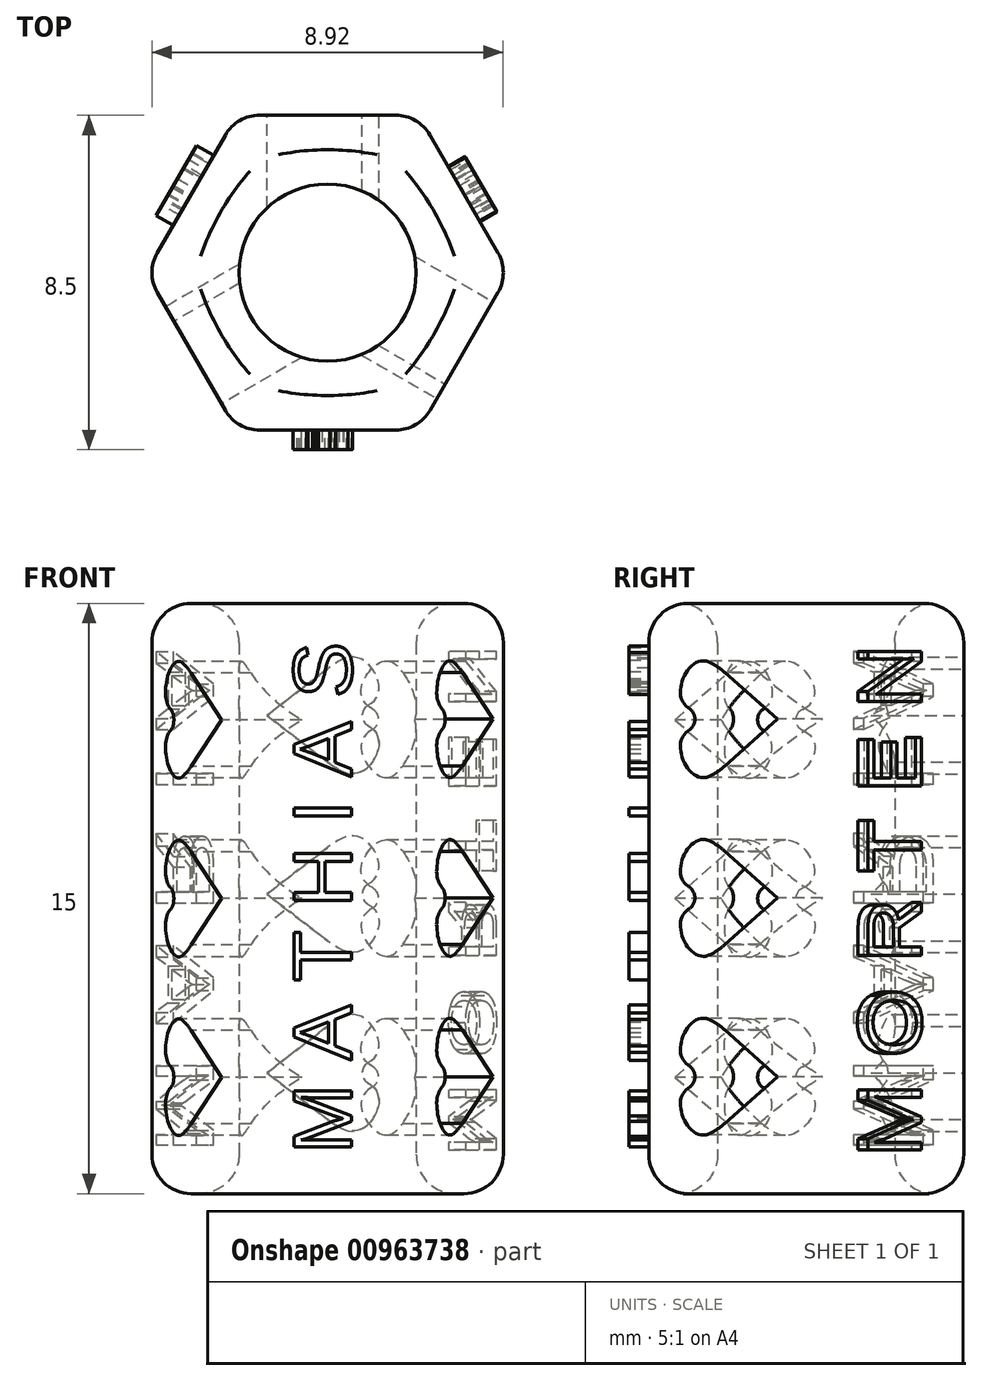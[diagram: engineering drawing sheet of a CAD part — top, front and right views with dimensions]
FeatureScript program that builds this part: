
annotation { "Feature Type Name" : "Feature", "Feature Type Description" : "" }
export const myFeature = defineFeature(function(context is Context, id is Id, definition is map)
    precondition{}
    {
        {
            var Q0;
            Q0=qCreatedBy(makeId("Top.planeOp"),FACE);
            var sketch = newSketch(context, id + "F0", { "sketchPlane" : qUnion([Q0])});
            skCircle(sketch, "E0", {"center": v(0, 0) * mm, "radius": 2.25 * mm});
            skCircle(sketch, "E1.cCircle", {"center": v(0, 0) * mm, "radius": 4 * mm, "construction": true});
            skLineSegment(sketch, "E1.0", {"start": v(2.3, -4) * mm, "end": v(-2.3, -4) * mm});
            skLineSegment(sketch, "E1.1", {"start": v(-2.3, -4) * mm, "end": v(-4.62, 0) * mm});
            skLineSegment(sketch, "E1.2", {"start": v(-4.62, 0) * mm, "end": v(-2.3, 4) * mm});
            skLineSegment(sketch, "E1.3", {"start": v(-2.3, 4) * mm, "end": v(2.3, 4) * mm});
            skLineSegment(sketch, "E1.4", {"start": v(2.3, 4) * mm, "end": v(4.62, 0) * mm});
            skLineSegment(sketch, "E1.5", {"start": v(4.62, 0) * mm, "end": v(2.3, -4) * mm});
            skPoint(sketch, "E1.0.midPoint", {"position": v(0, -4) * mm});
            skSolve(sketch);
        }
        {
            var Q0;
            Q0=makeQuery(id+"F0.imprint","IMPRINT",FACE,{"disambiguationData":[TD([[makeQuery(id+"F0.imprint","IMPRINT",EDGE,{"derivedFrom":sQuery(id+"F0.wireOp",EDGE,"E0")}),-1.0]])]});
            extrude(context, id + "F1", {"entities" : qUnion([Q0]), "depth" : 15 * mm, "offsetDistance" : 25 * mm});
        }
        {
            var Q0;
            Q0=makeQuery(id+"F1.opExtrude","SWEPT_FACE",FACE,{"disambiguationData":[OSD([sQuery(id+"F0.wireOp",EDGE,"E1.2")])]});
            var sketch = newSketch(context, id + "F2", { "sketchPlane" : qUnion([Q0])});
            skText(sketch, "E2", { "text": "M A R I A", "fontName": "Arimo-Regular.ttf"});
            skPoint(sketch, "E3", {"position": v(-2.3, 7.5) * mm});
            const initialGuessF2  = {"E2": [0.00092, 0.001, 0, 1, 0.00215]};
            skSetInitialGuess(sketch, initialGuessF2);
            skSolve(sketch);
        }
        {
            var Q0;
            Q0 = qSketchRegion(id + "F2", true);
            extrude(context, id + "F3", {"entities" : qUnion([Q0]), "operationType" : NewBodyOperationType.ADD, "depth" : 0.5 * mm, "offsetDistance" : 25 * mm});
        }
        {
            var Q0;
            Q0=makeQuery(id+"F1.opExtrude","SWEPT_FACE",FACE,{"disambiguationData":[OSD([sQuery(id+"F0.wireOp",EDGE,"E1.4")])]});
            var sketch = newSketch(context, id + "F4", { "sketchPlane" : qUnion([Q0])});
            skText(sketch, "E4", { "text": "M O R T E N", "fontName": "Arimo-Regular.ttf"});
            const initialGuessF4  = {"E4": [0.00078, 0.00093, 0, 1, 0.00164]};
            skSetInitialGuess(sketch, initialGuessF4);
            skSolve(sketch);
        }
        {
            var Q0;
            Q0 = qSketchRegion(id + "F4", true);
            extrude(context, id + "F5", {"entities" : qUnion([Q0]), "operationType" : NewBodyOperationType.ADD, "depth" : 0.5 * mm, "offsetDistance" : 25 * mm});
        }
        {
            var Q0;
            Q0=makeQuery(id+"F1.opExtrude","SWEPT_FACE",FACE,{"disambiguationData":[OSD([sQuery(id+"F0.wireOp",EDGE,"E1.0")])]});
            var sketch = newSketch(context, id + "F6", { "sketchPlane" : qUnion([Q0])});
            skText(sketch, "E5", { "text": "M A T H I A S", "fontName": "Arimo-Regular.ttf"});
            const initialGuessF6  = {"E5": [0.00061, 0.00102, 0, 1, 0.00153]};
            skSetInitialGuess(sketch, initialGuessF6);
            skSolve(sketch);
        }
        {
            var Q0;
            Q0 = qSketchRegion(id + "F6", true);
            extrude(context, id + "F7", {"entities" : qUnion([Q0]), "operationType" : NewBodyOperationType.ADD, "depth" : 0.5 * mm, "offsetDistance" : 25 * mm});
        }
        {
            var Q0;
            Q0=makeQuery(id+"F1.opExtrude","SWEPT_FACE",FACE,{"disambiguationData":[OSD([sQuery(id+"F0.wireOp",EDGE,"E1.1")])]});
            var sketch = newSketch(context, id + "F8", { "sketchPlane" : qUnion([Q0])});
            skLineSegment(sketch, "E6", {"start": v(2.3, 0) * mm, "end": v(-2.3, 15) * mm, "construction": true});
            skLineSegment(sketch, "E7", {"start": v(-2.3, 15) * mm, "end": v(0, 7.5) * mm, "construction": true});
            skLineSegment(sketch, "E8", {"start": v(0, 7.5) * mm, "end": v(1.54, 7.5) * mm, "construction": true});
            skLineSegment(sketch, "E9", {"start": v(1.54, 7.5) * mm, "end": v(0, 8.68) * mm});
            skFitSpline(sketch, "E10", {"points": [v(0, 8.68) * mm, v(-0.64, 8.98) * mm, v(-1.14, 8.68) * mm, v(-1.3, 8.14) * mm, v(-1.11, 7.81) * mm, v(-0.57, 7.6) * mm, v(0, 7.5) * mm], "startDerivative": vector(-3.48, 2.43) * mm, "endDerivative": vector(3.32, -0.48) * mm});
            skLineSegment(sketch, "E11.MirrorCS", {"start": v(1.54, 7.5) * mm, "end": v(0, 6.32) * mm});
            skFitSpline(sketch, "E12.MirrorCS", {"points": [v(0, 6.32) * mm, v(-0.64, 6.02) * mm, v(-1.14, 6.32) * mm, v(-1.3, 6.86) * mm, v(-1.11, 7.19) * mm, v(-0.57, 7.4) * mm, v(0, 7.5) * mm], "startDerivative": vector(-3.48, -2.43) * mm, "endDerivative": vector(3.32, 0.48) * mm});
            skLineSegment(sketch, "E13", {"start": v(2.3, 4.54) * mm, "end": v(-2.3, 19.54) * mm, "construction": true});
            skLineSegment(sketch, "E14", {"start": v(-2.3, 19.54) * mm, "end": v(0, 12.04) * mm, "construction": true});
            skLineSegment(sketch, "E15", {"start": v(0, 12.04) * mm, "end": v(1.54, 12.04) * mm, "construction": true});
            skLineSegment(sketch, "E16", {"start": v(1.54, 12.04) * mm, "end": v(0, 13.22) * mm});
            skFitSpline(sketch, "E17", {"points": [v(0, 13.22) * mm, v(-0.64, 13.52) * mm, v(-1.14, 13.22) * mm, v(-1.3, 12.68) * mm, v(-1.11, 12.35) * mm, v(-0.57, 12.14) * mm, v(0, 12.04) * mm], "startDerivative": vector(-3.48, 2.43) * mm, "endDerivative": vector(3.32, -0.48) * mm});
            skLineSegment(sketch, "E18.MirrorCS", {"start": v(1.54, 12.04) * mm, "end": v(0, 10.86) * mm});
            skFitSpline(sketch, "E19.MirrorCS", {"points": [v(0, 10.86) * mm, v(-0.64, 10.56) * mm, v(-1.14, 10.86) * mm, v(-1.3, 11.4) * mm, v(-1.11, 11.73) * mm, v(-0.57, 11.94) * mm, v(0, 12.04) * mm], "startDerivative": vector(-3.48, -2.43) * mm, "endDerivative": vector(3.32, 0.48) * mm});
            skLineSegment(sketch, "E20.MirrorCS", {"start": v(1.54, 2.96) * mm, "end": v(0, 1.78) * mm});
            skLineSegment(sketch, "E21.MirrorCS", {"start": v(1.54, 2.96) * mm, "end": v(0, 4.14) * mm});
            skFitSpline(sketch, "E22.MirrorCS", {"points": [v(0, 4.14) * mm, v(-0.64, 4.44) * mm, v(-1.14, 4.14) * mm, v(-1.3, 3.6) * mm, v(-1.11, 3.27) * mm, v(-0.57, 3.06) * mm, v(0, 2.96) * mm], "startDerivative": vector(-3.48, 2.43) * mm, "endDerivative": vector(3.32, -0.48) * mm});
            skFitSpline(sketch, "E23.MirrorCS", {"points": [v(0, 1.78) * mm, v(-0.64, 1.48) * mm, v(-1.14, 1.78) * mm, v(-1.3, 2.32) * mm, v(-1.11, 2.65) * mm, v(-0.57, 2.86) * mm, v(0, 2.96) * mm], "startDerivative": vector(-3.48, -2.43) * mm, "endDerivative": vector(3.32, 0.48) * mm});
            skSolve(sketch);
        }
        {
            var Q0;
            Q0=makeQuery(id+"F8.imprint","IMPRINT",FACE,{"disambiguationData":[TD([[makeQuery(id+"F8.imprint","IMPRINT",EDGE,{"derivedFrom":sQuery(id+"F8.wireOp",EDGE,"E20.MirrorCS")}),-1.0]])]});
            var Q1;
            Q1=makeQuery(id+"F8.imprint","IMPRINT",FACE,{"disambiguationData":[TD([[makeQuery(id+"F8.imprint","IMPRINT",EDGE,{"derivedFrom":sQuery(id+"F8.wireOp",EDGE,"E9")}),1.0]])]});
            var Q2;
            Q2=makeQuery(id+"F8.imprint","IMPRINT",FACE,{"disambiguationData":[TD([[makeQuery(id+"F8.imprint","IMPRINT",EDGE,{"derivedFrom":sQuery(id+"F8.wireOp",EDGE,"E16")}),1.0]])]});
            extrude(context, id + "F9", {"entities" : qUnion([Q0, Q1, Q2]), "operationType" : NewBodyOperationType.REMOVE, "oppositeDirection" : true, "depth" : 5 * mm, "offsetDistance" : 25 * mm});
        }
        {
            var Q0;
            Q0=makeQuery(id+"F1.opExtrude","SWEPT_FACE",FACE,{"disambiguationData":[OSD([sQuery(id+"F0.wireOp",EDGE,"E1.3")])]});
            var sketch = newSketch(context, id + "F10", { "sketchPlane" : qUnion([Q0])});
            skLineSegment(sketch, "E24", {"start": v(2.31, 0.1) * mm, "end": v(-2.3, 15.1) * mm, "construction": true});
            skLineSegment(sketch, "E25", {"start": v(-2.3, 15.1) * mm, "end": v(0, 7.6) * mm, "construction": true});
            skLineSegment(sketch, "E26", {"start": v(0, 7.6) * mm, "end": v(1.54, 7.6) * mm, "construction": true});
            skLineSegment(sketch, "E27", {"start": v(1.54, 7.6) * mm, "end": v(0, 8.8) * mm});
            skFitSpline(sketch, "E28", {"points": [v(0, 8.8) * mm, v(-0.64, 9.1) * mm, v(-1.14, 8.8) * mm, v(-1.3, 8.25) * mm, v(-1.1, 7.92) * mm, v(-0.57, 7.7) * mm, v(0, 7.6) * mm], "startDerivative": vector(-3.48, 2.43) * mm, "endDerivative": vector(3.32, -0.48) * mm});
            skLineSegment(sketch, "E29.MirrorCS", {"start": v(1.54, 7.6) * mm, "end": v(0, 6.43) * mm});
            skFitSpline(sketch, "E30.MirrorCS", {"points": [v(0, 6.43) * mm, v(-0.64, 6.12) * mm, v(-1.14, 6.43) * mm, v(-1.3, 6.97) * mm, v(-1.1, 7.3) * mm, v(-0.57, 7.5) * mm, v(0, 7.6) * mm], "startDerivative": vector(-3.48, -2.43) * mm, "endDerivative": vector(3.32, 0.48) * mm});
            skLineSegment(sketch, "E31", {"start": v(2.31, 4.65) * mm, "end": v(-2.3, 19.65) * mm, "construction": true});
            skLineSegment(sketch, "E32", {"start": v(-2.3, 19.65) * mm, "end": v(0, 12.15) * mm, "construction": true});
            skLineSegment(sketch, "E33", {"start": v(0, 12.15) * mm, "end": v(1.54, 12.15) * mm, "construction": true});
            skLineSegment(sketch, "E34", {"start": v(1.54, 12.15) * mm, "end": v(0, 13.33) * mm});
            skFitSpline(sketch, "E35", {"points": [v(0, 13.33) * mm, v(-0.64, 13.63) * mm, v(-1.14, 13.33) * mm, v(-1.3, 12.8) * mm, v(-1.1, 12.46) * mm, v(-0.57, 12.25) * mm, v(0, 12.15) * mm], "startDerivative": vector(-3.48, 2.43) * mm, "endDerivative": vector(3.32, -0.48) * mm});
            skLineSegment(sketch, "E36.MirrorCS", {"start": v(1.54, 12.15) * mm, "end": v(0, 10.97) * mm});
            skFitSpline(sketch, "E37.MirrorCS", {"points": [v(0, 10.97) * mm, v(-0.64, 10.67) * mm, v(-1.14, 10.97) * mm, v(-1.3, 11.5) * mm, v(-1.1, 11.84) * mm, v(-0.57, 12.05) * mm, v(0, 12.15) * mm], "startDerivative": vector(-3.48, -2.43) * mm, "endDerivative": vector(3.32, 0.48) * mm});
            skLineSegment(sketch, "E38.MirrorCS", {"start": v(1.54, 3.07) * mm, "end": v(0, 1.89) * mm});
            skLineSegment(sketch, "E39.MirrorCS", {"start": v(1.54, 3.07) * mm, "end": v(0, 4.25) * mm});
            skFitSpline(sketch, "E40.MirrorCS", {"points": [v(0, 4.25) * mm, v(-0.64, 4.55) * mm, v(-1.14, 4.25) * mm, v(-1.3, 3.71) * mm, v(-1.1, 3.38) * mm, v(-0.57, 3.17) * mm, v(0, 3.07) * mm], "startDerivative": vector(-3.48, 2.43) * mm, "endDerivative": vector(3.32, -0.48) * mm});
            skFitSpline(sketch, "E41.MirrorCS", {"points": [v(0, 1.89) * mm, v(-0.64, 1.58) * mm, v(-1.14, 1.89) * mm, v(-1.3, 2.43) * mm, v(-1.1, 2.76) * mm, v(-0.57, 2.97) * mm, v(0, 3.07) * mm], "startDerivative": vector(-3.48, -2.43) * mm, "endDerivative": vector(3.32, 0.48) * mm});
            skSolve(sketch);
        }
        {
            var Q0;
            Q0 = qSketchRegion(id + "F10", true);
            extrude(context, id + "F11", {"entities" : qUnion([Q0]), "operationType" : NewBodyOperationType.REMOVE, "oppositeDirection" : true, "depth" : 5 * mm, "offsetDistance" : 25 * mm});
        }
        {
            var Q0;
            Q0=makeQuery(id+"F1.opExtrude","SWEPT_FACE",FACE,{"disambiguationData":[OSD([sQuery(id+"F0.wireOp",EDGE,"E1.5")])]});
            var sketch = newSketch(context, id + "F12", { "sketchPlane" : qUnion([Q0])});
            skLineSegment(sketch, "E42", {"start": v(2.24, 0.01) * mm, "end": v(-2.38, 15.01) * mm, "construction": true});
            skLineSegment(sketch, "E43", {"start": v(-2.38, 15.01) * mm, "end": v(-0.07, 7.51) * mm, "construction": true});
            skLineSegment(sketch, "E44", {"start": v(-0.07, 7.51) * mm, "end": v(1.46, 7.51) * mm, "construction": true});
            skLineSegment(sketch, "E45", {"start": v(1.46, 7.51) * mm, "end": v(-0.07, 8.7) * mm});
            skFitSpline(sketch, "E46", {"points": [v(-0.07, 8.7) * mm, v(-0.72, 9) * mm, v(-1.21, 8.7) * mm, v(-1.38, 8.16) * mm, v(-1.18, 7.82) * mm, v(-0.64, 7.61) * mm, v(-0.07, 7.51) * mm], "startDerivative": vector(-3.48, 2.43) * mm, "endDerivative": vector(3.32, -0.48) * mm});
            skLineSegment(sketch, "E47.MirrorCS", {"start": v(1.46, 7.51) * mm, "end": v(-0.07, 6.33) * mm});
            skFitSpline(sketch, "E48.MirrorCS", {"points": [v(-0.07, 6.33) * mm, v(-0.72, 6.03) * mm, v(-1.21, 6.33) * mm, v(-1.38, 6.87) * mm, v(-1.18, 7.2) * mm, v(-0.64, 7.41) * mm, v(-0.07, 7.51) * mm], "startDerivative": vector(-3.48, -2.43) * mm, "endDerivative": vector(3.32, 0.48) * mm});
            skLineSegment(sketch, "E49", {"start": v(2.24, 4.55) * mm, "end": v(-2.38, 19.55) * mm, "construction": true});
            skLineSegment(sketch, "E50", {"start": v(-2.38, 19.55) * mm, "end": v(-0.07, 12.05) * mm, "construction": true});
            skLineSegment(sketch, "E51", {"start": v(-0.07, 12.05) * mm, "end": v(1.46, 12.05) * mm, "construction": true});
            skLineSegment(sketch, "E52", {"start": v(1.46, 12.05) * mm, "end": v(-0.07, 13.24) * mm});
            skFitSpline(sketch, "E53", {"points": [v(-0.07, 13.24) * mm, v(-0.72, 13.54) * mm, v(-1.21, 13.24) * mm, v(-1.38, 12.7) * mm, v(-1.18, 12.36) * mm, v(-0.64, 12.15) * mm, v(-0.07, 12.05) * mm], "startDerivative": vector(-3.48, 2.43) * mm, "endDerivative": vector(3.32, -0.48) * mm});
            skLineSegment(sketch, "E54.MirrorCS", {"start": v(1.46, 12.05) * mm, "end": v(-0.07, 10.87) * mm});
            skFitSpline(sketch, "E55.MirrorCS", {"points": [v(-0.07, 10.87) * mm, v(-0.72, 10.57) * mm, v(-1.21, 10.87) * mm, v(-1.38, 11.41) * mm, v(-1.18, 11.74) * mm, v(-0.64, 11.95) * mm, v(-0.07, 12.05) * mm], "startDerivative": vector(-3.48, -2.43) * mm, "endDerivative": vector(3.32, 0.48) * mm});
            skLineSegment(sketch, "E56.MirrorCS", {"start": v(1.46, 2.97) * mm, "end": v(-0.07, 1.8) * mm});
            skLineSegment(sketch, "E57.MirrorCS", {"start": v(1.46, 2.97) * mm, "end": v(-0.07, 4.16) * mm});
            skFitSpline(sketch, "E58.MirrorCS", {"points": [v(-0.07, 4.16) * mm, v(-0.72, 4.46) * mm, v(-1.21, 4.16) * mm, v(-1.38, 3.61) * mm, v(-1.18, 3.28) * mm, v(-0.64, 3.07) * mm, v(-0.07, 2.97) * mm], "startDerivative": vector(-3.48, 2.43) * mm, "endDerivative": vector(3.32, -0.48) * mm});
            skFitSpline(sketch, "E59.MirrorCS", {"points": [v(-0.07, 1.8) * mm, v(-0.72, 1.49) * mm, v(-1.21, 1.8) * mm, v(-1.38, 2.33) * mm, v(-1.18, 2.66) * mm, v(-0.64, 2.87) * mm, v(-0.07, 2.97) * mm], "startDerivative": vector(-3.48, -2.43) * mm, "endDerivative": vector(3.32, 0.48) * mm});
            skSolve(sketch);
        }
        {
            var Q0;
            Q0 = qSketchRegion(id + "F12", true);
            extrude(context, id + "F13", {"entities" : qUnion([Q0]), "operationType" : NewBodyOperationType.REMOVE, "oppositeDirection" : true, "depth" : 5 * mm, "offsetDistance" : 25 * mm});
        }
        {
            var Q0;
            Q0=makeQuery(id+"F1.opExtrude","CAP_FACE",FACE,{"disambiguationData":[OSD([sQuery(id+"F0.wireOp",EDGE,"E0"),sQuery(id+"F0.wireOp",EDGE,"E1.0"),sQuery(id+"F0.wireOp",EDGE,"E1.1"),sQuery(id+"F0.wireOp",EDGE,"E1.2"),sQuery(id+"F0.wireOp",EDGE,"E1.3"),sQuery(id+"F0.wireOp",EDGE,"E1.4"),sQuery(id+"F0.wireOp",EDGE,"E1.5")])],"isStart":false});
            var Q1;
            Q1=makeQuery(id+"F1.opExtrude","CAP_FACE",FACE,{"disambiguationData":[OSD([sQuery(id+"F0.wireOp",EDGE,"E0"),sQuery(id+"F0.wireOp",EDGE,"E1.0"),sQuery(id+"F0.wireOp",EDGE,"E1.1"),sQuery(id+"F0.wireOp",EDGE,"E1.2"),sQuery(id+"F0.wireOp",EDGE,"E1.3"),sQuery(id+"F0.wireOp",EDGE,"E1.4"),sQuery(id+"F0.wireOp",EDGE,"E1.5")])],"isStart":true});
            fillet(context, id + "F14", {"entities" : qUnion([Q0, Q1]), "radius" : 1 * mm, "tangentPropagation" : true, "allowEdgeOverflow" : false});
        }
        {
            var Q0;
            Q0=makeQuery(id+"F1.opExtrude","SWEPT_EDGE",EDGE,{"disambiguationData":[OSD([sQuery(id+"F0.wireOp",EDGE,"E1.0"),sQuery(id+"F0.wireOp",EDGE,"E1.5")])]});
            var Q1;
            Q1=makeQuery(id+"F1.opExtrude","SWEPT_EDGE",EDGE,{"disambiguationData":[OSD([sQuery(id+"F0.wireOp",EDGE,"E1.4"),sQuery(id+"F0.wireOp",EDGE,"E1.5")])]});
            var Q2;
            Q2=makeQuery(id+"F1.opExtrude","SWEPT_EDGE",EDGE,{"disambiguationData":[OSD([sQuery(id+"F0.wireOp",EDGE,"E1.3"),sQuery(id+"F0.wireOp",EDGE,"E1.4")])]});
            var Q3;
            Q3=makeQuery(id+"F1.opExtrude","SWEPT_EDGE",EDGE,{"disambiguationData":[OSD([sQuery(id+"F0.wireOp",EDGE,"E1.2"),sQuery(id+"F0.wireOp",EDGE,"E1.3")])]});
            var Q4;
            Q4=makeQuery(id+"F1.opExtrude","SWEPT_EDGE",EDGE,{"disambiguationData":[OSD([sQuery(id+"F0.wireOp",EDGE,"E1.1"),sQuery(id+"F0.wireOp",EDGE,"E1.2")])]});
            var Q5;
            Q5=makeQuery(id+"F1.opExtrude","SWEPT_EDGE",EDGE,{"disambiguationData":[OSD([sQuery(id+"F0.wireOp",EDGE,"E1.0"),sQuery(id+"F0.wireOp",EDGE,"E1.1")])]});
            fillet(context, id + "F15", {"entities" : qUnion([Q0, Q1, Q2, Q3, Q4, Q5]), "radius" : 1 * mm, "tangentPropagation" : true, "allowEdgeOverflow" : false});
        }
        {
            var Q0;
            Q0=makeQuery(id+"F9.boolean.opBoolean","COPY",EDGE,{"derivedFrom":makeQuery(id+"F9.opExtrude","SWEPT_EDGE",EDGE,{"disambiguationData":[OSD([sQuery(id+"F8.wireOp",EDGE,"E17"),sQuery(id+"F8.wireOp",EDGE,"E19.MirrorCS")])]})});
            var Q1;
            Q1=makeQuery(id+"F9.boolean.opBoolean","COPY",EDGE,{"derivedFrom":makeQuery(id+"F9.opExtrude","SWEPT_EDGE",EDGE,{"disambiguationData":[OSD([sQuery(id+"F8.wireOp",EDGE,"E10"),sQuery(id+"F8.wireOp",EDGE,"E12.MirrorCS")])]})});
            var Q2;
            Q2=makeQuery(id+"F9.boolean.opBoolean","COPY",EDGE,{"derivedFrom":makeQuery(id+"F9.opExtrude","SWEPT_EDGE",EDGE,{"disambiguationData":[OSD([sQuery(id+"F8.wireOp",EDGE,"E22.MirrorCS"),sQuery(id+"F8.wireOp",EDGE,"E23.MirrorCS")])]})});
            var Q3;
            Q3=makeQuery(id+"F11.boolean.opBoolean","COPY",EDGE,{"derivedFrom":makeQuery(id+"F11.opExtrude","SWEPT_EDGE",EDGE,{"disambiguationData":[OSD([sQuery(id+"F10.wireOp",EDGE,"E40.MirrorCS"),sQuery(id+"F10.wireOp",EDGE,"E41.MirrorCS")])]})});
            var Q4;
            Q4=makeQuery(id+"F11.boolean.opBoolean","COPY",EDGE,{"derivedFrom":makeQuery(id+"F11.opExtrude","SWEPT_EDGE",EDGE,{"disambiguationData":[OSD([sQuery(id+"F10.wireOp",EDGE,"E28"),sQuery(id+"F10.wireOp",EDGE,"E30.MirrorCS")])]})});
            var Q5;
            Q5=makeQuery(id+"F11.boolean.opBoolean","COPY",EDGE,{"derivedFrom":makeQuery(id+"F11.opExtrude","SWEPT_EDGE",EDGE,{"disambiguationData":[OSD([sQuery(id+"F10.wireOp",EDGE,"E35"),sQuery(id+"F10.wireOp",EDGE,"E37.MirrorCS")])]})});
            var Q6;
            Q6=makeQuery(id+"F13.boolean.opBoolean","COPY",EDGE,{"derivedFrom":makeQuery(id+"F13.opExtrude","SWEPT_EDGE",EDGE,{"disambiguationData":[OSD([sQuery(id+"F12.wireOp",EDGE,"E58.MirrorCS"),sQuery(id+"F12.wireOp",EDGE,"E59.MirrorCS")])]})});
            var Q7;
            Q7=makeQuery(id+"F13.boolean.opBoolean","COPY",EDGE,{"derivedFrom":makeQuery(id+"F13.opExtrude","SWEPT_EDGE",EDGE,{"disambiguationData":[OSD([sQuery(id+"F12.wireOp",EDGE,"E46"),sQuery(id+"F12.wireOp",EDGE,"E48.MirrorCS")])]})});
            var Q8;
            Q8=makeQuery(id+"F13.boolean.opBoolean","COPY",EDGE,{"derivedFrom":makeQuery(id+"F13.opExtrude","SWEPT_EDGE",EDGE,{"disambiguationData":[OSD([sQuery(id+"F12.wireOp",EDGE,"E53"),sQuery(id+"F12.wireOp",EDGE,"E55.MirrorCS")])]})});
            fillet(context, id + "F16", {"entities" : qUnion([Q0, Q1, Q2, Q3, Q4, Q5, Q6, Q7, Q8]), "radius" : 0.3 * mm, "tangentPropagation" : true, "allowEdgeOverflow" : false});
        }
    });
